# Revit family: BEG-91008
name_source: partatom
category: Dispositifs d'éclairage
revit_build: Autodesk Revit 2015 (Build: 20140606_1530(x64)
units: mm (PartAtom-declared; Revit-internal decimal feet)

## types (1)
- BEG-91008
    Artikel-Nummer = 91008
    Ausgabetyp = Schalten
    Code d'assemblage = D5010200
    Commentaires du type = LC-plus 280-weiß  BEG Luxomat Bewegungsmelder
    Elévation par défaut = 250 cm
    Fabricant = B.E.G
    IP = 44
    Image du type = 91008.jpg
    Klasse = 2
    Marke = LUXOMAT
    Max Montagehöhe empfohlen = 300 cm
    Modèle = LC-plus 280, weiß
    Montagehöhe max = 300 cm
    Montge Anleitung = Aufputz Version
    Relais = 10A
    SPANNUNG = 110-240 V AC
    Schaltleistung Kanal Cos ɸ =0,5 = 500VA
    Schaltleistung Kanal Cos ɸ =1 = 2000W
    Schaltleistung Kanal LED = 250W
    Typische Leistungsaufnahme = 0,39W
    URL = http://www.luxomat.com
    Umgebungstemperatur = -25°C bis +50°C

## geometry (parser evidence)
native form markers: Extrusion x2
no freeform markers — native parametric forms only
